FREECAD ASSEMBLY — COMPONENT RECIPES ("sway_platform")

This assembly document has 28 components, labeled P0..P27 below (a component is one placed body or linked part). 9 of them carry a construction recipe — the FreeCAD feature program that regenerates the part from scratch, quoted from this document or its linked companion documents; the rest are supplied as boundary geometry only. No exploded tour is included for this assembly.
COMPONENT P0 — geometry summary ("BK12"; no construction recipe available for this part):
  bounding box: 60.0 x 43.0 x 35.0 mm
  tessellated surface: 293,432 triangles
  volume: 48234 mm^3 (53% of its bounding box)
COMPONENT P1 — geometry summary ("DSG16H"; no construction recipe available for this part):
  bounding box: 52.0 x 40.0 x 40.0 mm
  tessellated surface: 114,100 triangles
  volume: 50009 mm^3 (60% of its bounding box)
  symmetry: mirror-symmetric across its x mid-plane
COMPONENT P2 — recipe-attached ("DSG16H_to_SH25", a linked part whose construction recipe lives in a companion FreeCAD document of the same project; that document's serialized recipe follows).
Construction recipe (the companion document, serialized — sketch geometry with constraints, then the solid features built on it; lengths are millimeters unless a unit is written):

FCSTD DOCUMENT  (FreeCAD 1.0R39109 (Git))
Label: DSG16H_to_SH25
License: All rights reserved
LicenseURL: https://en.wikipedia.org/wiki/All_rights_reserved
objects: Sketcher::SketchObject×4, PartDesign::Pocket×3, PartDesign::Pad×1, PartDesign::Fillet×1, PartDesign::Body×1
note: 24 computed .brp shape members not serialized (recipe doc carries the construction recipe); baked Part::Feature solids carry a one-line shape summary decoded from their .brp

FEATURE [Sketcher::SketchObject] Sketch
  ArcFitTolerance = 1e-06
  AttachmentSupport = -> [XY_Plane]
  FullyConstrained = true
  MakeInternals = false
  MapMode = 5
  sketch-geometry (19):
    g0: LineSegment StartX=50 StartY=0 StartZ=0 EndX=50 EndY=38 EndZ=0
    g1: LineSegment StartX=0 StartY=38 StartZ=0 EndX=0 EndY=0 EndZ=0
    g2: LineSegment [constr] StartX=5 StartY=7 StartZ=0 EndX=45 EndY=7 EndZ=0
    g3: LineSegment [constr] StartX=45 StartY=7 StartZ=0 EndX=45 EndY=31 EndZ=0
    g4: LineSegment [constr] StartX=45 StartY=31 StartZ=0 EndX=5 EndY=31 EndZ=0
    g5: LineSegment [constr] StartX=5 StartY=31 StartZ=0 EndX=5 EndY=7 EndZ=0
    g6: LineSegment [constr] StartX=0 StartY=0 StartZ=0 EndX=5 EndY=7 EndZ=0
    g7: LineSegment [constr] StartX=5 StartY=31 StartZ=0 EndX=-9e-16 EndY=38 EndZ=0
    g8: LineSegment [constr] StartX=45 StartY=31 StartZ=0 EndX=50 EndY=38 EndZ=0
    g9: Circle CenterX=5 CenterY=31 CenterZ=0 NormalX=0 NormalY=0 NormalZ=1 AngleXU=0 Radius=2.8
    g10: Circle CenterX=45 CenterY=31 CenterZ=0 NormalX=0 NormalY=0 NormalZ=1 AngleXU=0 Radius=2.8
    g11: Circle CenterX=45 CenterY=7 CenterZ=0 NormalX=0 NormalY=0 NormalZ=1 AngleXU=0 Radius=2.8
    g12: Circle CenterX=5 CenterY=7 CenterZ=0 NormalX=0 NormalY=0 NormalZ=1 AngleXU=0 Radius=2.8
    g13: LineSegment StartX=0 StartY=38 StartZ=0 EndX=13 EndY=54 EndZ=0
    g14: LineSegment StartX=13 StartY=54 StartZ=0 EndX=37 EndY=54 EndZ=0
    g15: LineSegment StartX=37 StartY=54 StartZ=0 EndX=50 EndY=38 EndZ=0
    g16: LineSegment StartX=50 StartY=0 StartZ=0 EndX=37 EndY=-16 EndZ=0
    g17: LineSegment StartX=37 StartY=-16 StartZ=0 EndX=13 EndY=-16 EndZ=0
    g18: LineSegment StartX=13 StartY=-16 StartZ=0 EndX=0 EndY=1.8e-15 EndZ=0
  constraints (49):
    c: Vertical(g0)
    c: Vertical(g1)
    c: Distance(g0,g1) = 50
    c: Distance(g1,g1) = 38
    c: Coincident(g2,g3)
    c: Coincident(g3,g4)
    c: Coincident(g4,g5)
    c: Coincident(g5,g2)
    c: Horizontal(g2)
    c: Horizontal(g4)
    c: Vertical(g3)
    c: Vertical(g5)
    c: Distance(g3,g5) = 40
    c: Distance(g2,g4) = 24
    c: Coincident(g6,g2)
    c: Coincident(g7,g4)
    c: Coincident(g8,g3)
    c: Coincident(g8,g0)
    c: Equal(g8,g7)
    c: Equal(g7,g6)
    c: Coincident(g9,g4)
    c: Coincident(g10,g3)
    c: Coincident(g11,g2)
    c: Coincident(g12,g2)
    c: Equal(g12,g9)
    c: Equal(g12,g11)
    c: Equal(g12,g10)
    c: Diameter(g12) = 5.6
    c: Equal(g0,g1)
    c: Coincident(g1,g-1)
    c: Coincident(g6,g1)
    c: PointOnObject(g0,g-1)
    c: Coincident(g7,g1)
    c: Coincident(g13,g1)
    c: Coincident(g14,g13)
    c: Horizontal(g14)
    c: Coincident(g15,g14)
    c: Coincident(g15,g0)
    c: Coincident(g16,g0)
    c: Coincident(g17,g16)
    c: Horizontal(g17)
    c: Coincident(g18,g17)
    c: Coincident(g18,g1)
    c: DistanceY(g17,g13) = 70
    c: Equal(g14,g17)
    c: Equal(g13,g15)
    c: Equal(g15,g16)
    c: Equal(g16,g18)
    c: DistanceX(g14,g14) = 24
FEATURE [PartDesign::Pad] Pad
  Direction = (0,0,1)
  Length = 12
  Length2 = 10
  Profile = -> Sketch
  ReferenceAxis = -> Sketch [N_Axis]
  Refine = true
  Suppressed = false
  Type = 0
FEATURE [Sketcher::SketchObject] Sketch001
  ArcFitTolerance = 1e-06
  AttachmentSupport = -> [Pad]
  FullyConstrained = true
  MakeInternals = false
  MapMode = 5
  Placement = pos=(0,0,12) rot=(0,0,1;0rad)
  sketch-geometry (2):
    g0: Circle CenterX=25 CenterY=47 CenterZ=0 NormalX=0 NormalY=0 NormalZ=1 AngleXU=0 Radius=3.3
    g1: Circle CenterX=25 CenterY=-9 CenterZ=0 NormalX=0 NormalY=0 NormalZ=1 AngleXU=0 Radius=3.3
  constraints (6):
    c: DistanceY(g1,g0) = 56
    c: DistanceX(g1) = 25
    c: DistanceX(g1,g0) = 0
    c: DistanceY(g1,g-1) = 9
    c: Equal(g1,g0)
    c: Diameter(g1) = 6.6
FEATURE [PartDesign::Pocket] Pocket
  BaseFeature = -> Pad
  Direction = (0,0,-1)
  Length = 5
  Length2 = 5
  Profile = -> Sketch001
  ReferenceAxis = -> Sketch001 [N_Axis]
  Refine = true
  Suppressed = false
  Type = 1
FEATURE [Sketcher::SketchObject] Sketch002
  ArcFitTolerance = 1e-06
  AttachmentSupport = -> [Pocket]
  FullyConstrained = true
  MakeInternals = false
  MapMode = 5
  Placement = pos=(0,0,0) rot=(1,0,0;3.14159rad)
  expr: Constraints[0] = Sketch001.Constraints[0]
  expr: Constraints[1] = Sketch001.Constraints[1]
  expr: Constraints[2] = Sketch001.Constraints[2]
  expr: Constraints[5] = Sketch001.Constraints[5]
  sketch-geometry (16):
    g0: Circle [constr] CenterX=25 CenterY=9 CenterZ=0 NormalX=0 NormalY=0 NormalZ=1 AngleXU=0 Radius=3.3
    g1: Circle [constr] CenterX=25 CenterY=-47 CenterZ=0 NormalX=0 NormalY=0 NormalZ=1 AngleXU=0 Radius=3.3
    g2: LineSegment StartX=27.9734 StartY=-52.15 StartZ=0 EndX=30.9467 EndY=-47 EndZ=0
    g3: LineSegment StartX=30.9467 StartY=-47 StartZ=0 EndX=27.9734 EndY=-41.85 EndZ=0
    g4: LineSegment StartX=27.9734 StartY=-41.85 StartZ=0 EndX=22.0266 EndY=-41.85 EndZ=0
    g5: LineSegment StartX=22.0266 StartY=-41.85 StartZ=0 EndX=19.0533 EndY=-47 EndZ=0
    g6: LineSegment StartX=19.0533 StartY=-47 StartZ=0 EndX=22.0266 EndY=-52.15 EndZ=0
    g7: LineSegment StartX=22.0266 StartY=-52.15 StartZ=0 EndX=27.9734 EndY=-52.15 EndZ=0
    g8: Circle [constr] CenterX=25 CenterY=-47 CenterZ=0 NormalX=0 NormalY=0 NormalZ=1 AngleXU=0 Radius=5.94671
    g9: LineSegment StartX=27.9734 StartY=3.85 StartZ=0 EndX=30.9467 EndY=9 EndZ=0
    g10: LineSegment StartX=30.9467 StartY=9 StartZ=0 EndX=27.9734 EndY=14.15 EndZ=0
    g11: LineSegment StartX=27.9734 StartY=14.15 StartZ=0 EndX=22.0266 EndY=14.15 EndZ=0
    g12: LineSegment StartX=22.0266 StartY=14.15 StartZ=0 EndX=19.0533 EndY=9 EndZ=0
    g13: LineSegment StartX=19.0533 StartY=9 StartZ=0 EndX=22.0266 EndY=3.85 EndZ=0
    g14: LineSegment StartX=22.0266 StartY=3.85 StartZ=0 EndX=27.9734 EndY=3.85 EndZ=0
    g15: Circle [constr] CenterX=25 CenterY=9 CenterZ=0 NormalX=0 NormalY=0 NormalZ=1 AngleXU=0 Radius=5.94671
  constraints (38):
    c: DistanceY(g1,g0) = 56
    c: DistanceX(g1) = 25
    c: DistanceX(g1,g0) = 0
    c: DistanceY(g1,g-1) = 47
    c: Equal(g1,g0)
    c: Diameter(g1) = 6.6
    c: Coincident(g2,g3)
    c: Coincident(g3,g4)
    c: Coincident(g4,g5)
    c: Coincident(g5,g6)
    c: Coincident(g6,g7)
    c: Coincident(g7,g2)
    c: Equal(g2, g3-g7) x5
    c: PointOnObject(g2,g8)
    c: PointOnObject(g3,g8)
    c: PointOnObject(g4,g8)
    c: PointOnObject(g5,g8)
    c: PointOnObject(g6,g8)
    c: PointOnObject(g7,g8)
    c: Coincident(g8,g1)
    c: Distance(g4,g2) = 10.3
    c: Horizontal(g4)
    c: Coincident(g9,g10)
    c: Coincident(g10,g11)
    c: Coincident(g11,g12)
    c: Coincident(g12,g13)
    c: Coincident(g13,g14)
    c: Coincident(g14,g9)
    c: Equal(g9, g10-g14) x5
    c: PointOnObject(g9,g15)
    c: PointOnObject(g10,g15)
    c: PointOnObject(g11,g15)
    c: PointOnObject(g12,g15)
    c: PointOnObject(g13,g15)
    c: PointOnObject(g14,g15)
    c: Coincident(g15,g0)
    c: Horizontal(g11)
    c: Equal(g14,g4)
FEATURE [PartDesign::Pocket] Pocket001
  BaseFeature = -> Pocket
  Direction = (0,0,1)
  Length = 6
  Length2 = 5
  Profile = -> Sketch002
  ReferenceAxis = -> Sketch002 [N_Axis]
  Refine = true
  Suppressed = false
  Type = 0
FEATURE [PartDesign::Fillet] Fillet
  Base = -> Pocket001 [Edge46,Edge44,Edge8,Edge45,Edge43,Edge5,Edge1,Edge2]
  BaseFeature = -> Pocket001
  Radius = 4
  Refine = true
  SupportTransform = false
  Suppressed = false
  UseAllEdges = false
FEATURE [Sketcher::SketchObject] Sketch003
  ArcFitTolerance = 1e-06
  AttachmentSupport = -> [Fillet]
  FullyConstrained = true
  MakeInternals = false
  MapMode = 5
  Placement = pos=(0,0,12) rot=(0,0,1;0rad)
  sketch-geometry (4):
    g0: LineSegment StartX=37 StartY=54 StartZ=0 EndX=37 EndY=-16 EndZ=0
    g1: LineSegment StartX=37 StartY=-16 StartZ=0 EndX=50 EndY=-16 EndZ=0
    g2: LineSegment StartX=50 StartY=-16 StartZ=0 EndX=50 EndY=54 EndZ=0
    g3: LineSegment StartX=50 StartY=54 StartZ=0 EndX=37 EndY=54 EndZ=0
  constraints (12):
    c: Coincident(g0,g1)
    c: Coincident(g1,g2)
    c: Coincident(g2,g3)
    c: Coincident(g3,g0)
    c: Vertical(g0)
    c: Vertical(g2)
    c: Horizontal(g1)
    c: Horizontal(g3)
    c: Distance(g0,g2) = 13
    c: DistanceX(g1) = 50
    c: DistanceY(g0) = -16
    c: DistanceY(g0,g0) = 70
FEATURE [PartDesign::Pocket] Pocket002
  BaseFeature = -> Fillet
  Direction = (0,0,-1)
  Length = 5
  Length2 = 5
  Profile = -> Sketch003
  ReferenceAxis = -> Sketch003 [N_Axis]
  Refine = true
  Suppressed = false
  Type = 0
FEATURE [PartDesign::Body] Body  label="DSG16H_to_SH25"
  AllowCompound = false
  Group = -> [Sketch,Pad,Sketch001,Pocket,Sketch002,Pocket001,Fillet,Sketch003,Pocket002]
  Origin = -> Origin
  Tip = -> Pocket002
COMPONENT P3 — geometry summary ("SC25UU_000"; no construction recipe available for this part):
  bounding box: 76.0 x 67.0 x 51.5 mm
  tessellated surface: 5,480 triangles
  volume: 179746 mm^3 (69% of its bounding box)
  symmetry: 2-fold rotationally symmetric about the z axis; mirror-symmetric across its y mid-plane
COMPONENT P4 — geometry summary ("SC25UU_001"; no construction recipe available for this part):
  bounding box: 76.0 x 67.0 x 51.5 mm
  tessellated surface: 5,480 triangles
  volume: 179746 mm^3 (69% of its bounding box)
  symmetry: 2-fold rotationally symmetric about the z axis; mirror-symmetric across its y mid-plane
COMPONENT P5 — geometry summary ("SC25UU_002"; no construction recipe available for this part):
  bounding box: 76.0 x 67.0 x 51.5 mm
  tessellated surface: 5,480 triangles
  volume: 179746 mm^3 (69% of its bounding box)
  symmetry: 2-fold rotationally symmetric about the z axis; mirror-symmetric across its y mid-plane
COMPONENT P6 — geometry summary ("SC25UU_003"; no construction recipe available for this part):
  bounding box: 76.0 x 67.0 x 51.5 mm
  tessellated surface: 5,480 triangles
  volume: 179746 mm^3 (69% of its bounding box)
  symmetry: 2-fold rotationally symmetric about the z axis; mirror-symmetric across its y mid-plane
COMPONENT P7 — recipe-attached ("SC25UU_to_SH25_001", a linked part whose construction recipe lives in a companion FreeCAD document of the same project; that document's serialized recipe follows).
Construction recipe (the companion document, serialized — sketch geometry with constraints, then the solid features built on it; lengths are millimeters unless a unit is written):

FCSTD DOCUMENT  (FreeCAD 1.0R39109 (Git))
Label: SC25UU_to_SH25
License: All rights reserved
LicenseURL: https://en.wikipedia.org/wiki/All_rights_reserved
objects: Sketcher::SketchObject×3, PartDesign::Pocket×2, PartDesign::Pad×1, PartDesign::Fillet×1, PartDesign::Body×1
note: 19 computed .brp shape members not serialized (recipe doc carries the construction recipe); baked Part::Feature solids carry a one-line shape summary decoded from their .brp

FEATURE [Sketcher::SketchObject] Sketch
  ArcFitTolerance = 1e-06
  AttachmentSupport = -> [XY_Plane]
  FullyConstrained = true
  MakeInternals = false
  MapMode = 5
  sketch-geometry (19):
    g0: LineSegment StartX=76 StartY=0 StartZ=0 EndX=76 EndY=67 EndZ=0
    g1: LineSegment StartX=0 StartY=67 StartZ=0 EndX=0 EndY=0 EndZ=0
    g2: LineSegment [constr] StartX=11 StartY=58.5 StartZ=0 EndX=11 EndY=8.5 EndZ=0
    g3: LineSegment [constr] StartX=11 StartY=8.5 StartZ=0 EndX=65 EndY=8.5 EndZ=0
    g4: LineSegment [constr] StartX=65 StartY=8.5 StartZ=0 EndX=65 EndY=58.5 EndZ=0
    g5: LineSegment [constr] StartX=65 StartY=58.5 StartZ=0 EndX=11 EndY=58.5 EndZ=0
    g6: Circle CenterX=11 CenterY=58.5 CenterZ=0 NormalX=0 NormalY=0 NormalZ=1 AngleXU=0 Radius=4.3
    g7: Circle CenterX=65 CenterY=58.5 CenterZ=0 NormalX=0 NormalY=0 NormalZ=1 AngleXU=0 Radius=4.3
    g8: Circle CenterX=65 CenterY=8.5 CenterZ=0 NormalX=0 NormalY=0 NormalZ=1 AngleXU=0 Radius=4.3
    g9: Circle CenterX=11 CenterY=8.5 CenterZ=0 NormalX=0 NormalY=0 NormalZ=1 AngleXU=0 Radius=4.3
    g10: LineSegment [constr] StartX=0 StartY=0 StartZ=0 EndX=11 EndY=8.5 EndZ=0
    g11: LineSegment [constr] StartX=65 StartY=58.5 StartZ=0 EndX=76 EndY=67 EndZ=0
    g12: LineSegment [constr] StartX=11 StartY=58.5 StartZ=0 EndX=0 EndY=67 EndZ=0
    g13: LineSegment StartX=0 StartY=67 StartZ=0 EndX=26 EndY=68.5 EndZ=0
    g14: LineSegment StartX=26 StartY=68.5 StartZ=0 EndX=50 EndY=68.5 EndZ=0
    g15: LineSegment StartX=50 StartY=68.5 StartZ=0 EndX=76 EndY=67 EndZ=0
    g16: LineSegment StartX=0 StartY=0 StartZ=0 EndX=26 EndY=-1.5 EndZ=0
    g17: LineSegment StartX=26 StartY=-1.5 StartZ=0 EndX=50 EndY=-1.5 EndZ=0
    g18: LineSegment StartX=50 StartY=-1.5 StartZ=0 EndX=76 EndY=0 EndZ=0
  constraints (49):
    c: Vertical(g0)
    c: Vertical(g1)
    c: Distance(g0,g1) = 76
    c: Distance(g1,g1) = 67
    c: Coincident(g2,g3)
    c: Coincident(g3,g4)
    c: Coincident(g4,g5)
    c: Coincident(g5,g2)
    c: Vertical(g2)
    c: Vertical(g4)
    c: Horizontal(g3)
    c: Horizontal(g5)
    c: Distance(g2,g4) = 54
    c: Distance(g3,g5) = 50
    c: Coincident(g6,g2)
    c: Coincident(g7,g4)
    c: Coincident(g8,g3)
    c: Coincident(g9,g2)
    c: Equal(g7,g8)
    c: Equal(g7,g9)
    c: Equal(g7,g6)
    c: Diameter(g7) = 8.6
    c: Coincident(g10,g2)
    c: Coincident(g11,g4)
    c: Coincident(g11,g0)
    c: Coincident(g12,g2)
    c: Equal(g12,g10)
    c: Equal(g12,g11)
    c: Coincident(g13,g1)
    c: Coincident(g14,g13)
    c: Horizontal(g14)
    c: Coincident(g15,g14)
    c: Coincident(g15,g0)
    c: Coincident(g16,g1)
    c: Coincident(g17,g16)
    c: Horizontal(g17)
    c: Coincident(g18,g17)
    c: Coincident(g18,g0)
    c: DistanceX(g17,g17) = 24
    c: Equal(g17,g14)
    c: Equal(g13,g15)
    c: Equal(g15,g18)
    c: Equal(g18,g16)
    c: Coincident(g1,g10)
    c: Coincident(g1,g-1)
    c: Coincident(g12,g1)
    c: PointOnObject(g0,g-1)
    c: Equal(g0,g1)
    c: DistanceY(g16,g13) = 70
FEATURE [PartDesign::Pad] Pad
  Direction = (0,0,1)
  Length = 10
  Length2 = 10
  Profile = -> Sketch
  ReferenceAxis = -> Sketch [N_Axis]
  Refine = true
  Suppressed = false
  Type = 0
FEATURE [Sketcher::SketchObject] Sketch001
  ArcFitTolerance = 1e-06
  AttachmentSupport = -> [Pad]
  FullyConstrained = true
  MakeInternals = false
  MapMode = 5
  Placement = pos=(0,0,10) rot=(0,0,1;0rad)
  sketch-geometry (2):
    g0: Circle CenterX=38 CenterY=61.5 CenterZ=0 NormalX=0 NormalY=0 NormalZ=1 AngleXU=0 Radius=3.3
    g1: Circle CenterX=38 CenterY=5.5 CenterZ=0 NormalX=0 NormalY=0 NormalZ=1 AngleXU=0 Radius=3.3
  constraints (6):
    c: DistanceY(g1,g0) = 56
    c: Equal(g1,g0)
    c: Diameter(g1) = 6.6
    c: DistanceY(g1) = 5.5
    c: DistanceX(g1) = 38
    c: DistanceX(g0,g1) = 0
FEATURE [PartDesign::Pocket] Pocket
  BaseFeature = -> Pad
  Direction = (0,0,-1)
  Length = 5
  Length2 = 5
  Profile = -> Sketch001
  ReferenceAxis = -> Sketch001 [N_Axis]
  Refine = true
  Suppressed = false
  Type = 1
FEATURE [Sketcher::SketchObject] Sketch002
  ArcFitTolerance = 1e-06
  AttachmentSupport = -> [Pocket]
  FullyConstrained = true
  MakeInternals = false
  MapMode = 5
  Placement = pos=(0,0,0) rot=(1,0,0;3.14159rad)
  expr: Constraints[2] = Sketch001.Constraints[2]
  expr: Constraints[4] = Sketch001.Constraints[4]
  expr: Constraints[5] = Sketch001.Constraints[5]
  sketch-geometry (16):
    g0: Circle [constr] CenterX=38 CenterY=-61.5 CenterZ=0 NormalX=0 NormalY=0 NormalZ=1 AngleXU=0 Radius=3.3
    g1: Circle [constr] CenterX=38 CenterY=-5.5 CenterZ=0 NormalX=0 NormalY=0 NormalZ=1 AngleXU=0 Radius=3.3
    g2: LineSegment StartX=40.9734 StartY=-10.65 StartZ=0 EndX=43.9467 EndY=-5.5 EndZ=0
    g3: LineSegment StartX=43.9467 StartY=-5.5 StartZ=0 EndX=40.9734 EndY=-0.35 EndZ=0
    g4: LineSegment StartX=40.9734 StartY=-0.35 StartZ=0 EndX=35.0266 EndY=-0.35 EndZ=0
    g5: LineSegment StartX=35.0266 StartY=-0.35 StartZ=0 EndX=32.0533 EndY=-5.5 EndZ=0
    g6: LineSegment StartX=32.0533 StartY=-5.5 StartZ=0 EndX=35.0266 EndY=-10.65 EndZ=0
    g7: LineSegment StartX=35.0266 StartY=-10.65 StartZ=0 EndX=40.9734 EndY=-10.65 EndZ=0
    g8: Circle [constr] CenterX=38 CenterY=-5.5 CenterZ=0 NormalX=0 NormalY=0 NormalZ=1 AngleXU=0 Radius=5.94671
    g9: LineSegment StartX=43.9467 StartY=-61.5 StartZ=0 EndX=40.9734 EndY=-56.35 EndZ=0
    g10: LineSegment StartX=40.9734 StartY=-56.35 StartZ=0 EndX=35.0266 EndY=-56.35 EndZ=0
    g11: LineSegment StartX=35.0266 StartY=-56.35 StartZ=0 EndX=32.0533 EndY=-61.5 EndZ=0
    g12: LineSegment StartX=32.0533 StartY=-61.5 StartZ=0 EndX=35.0266 EndY=-66.65 EndZ=0
    g13: LineSegment StartX=35.0266 StartY=-66.65 StartZ=0 EndX=40.9734 EndY=-66.65 EndZ=0
    g14: LineSegment StartX=40.9734 StartY=-66.65 StartZ=0 EndX=43.9467 EndY=-61.5 EndZ=0
    g15: Circle [constr] CenterX=38 CenterY=-61.5 CenterZ=0 NormalX=0 NormalY=0 NormalZ=1 AngleXU=0 Radius=5.94671
  constraints (38):
    c: DistanceY(g1,g0) = -56
    c: Equal(g1,g0)
    c: Diameter(g1) = 6.6
    c: DistanceY(g1) = -5.5
    c: DistanceX(g1) = 38
    c: DistanceX(g0,g1) = 0
    c: Coincident(g2,g3)
    c: Coincident(g3,g4)
    c: Coincident(g4,g5)
    c: Coincident(g5,g6)
    c: Coincident(g6,g7)
    c: Coincident(g7,g2)
    c: Equal(g2, g3-g7) x5
    c: PointOnObject(g2,g8)
    c: PointOnObject(g3,g8)
    c: PointOnObject(g4,g8)
    c: PointOnObject(g5,g8)
    c: PointOnObject(g6,g8)
    c: PointOnObject(g7,g8)
    c: Coincident(g8,g1)
    c: Coincident(g9,g10)
    c: Coincident(g10,g11)
    c: Coincident(g11,g12)
    c: Coincident(g12,g13)
    c: Coincident(g13,g14)
    c: Coincident(g14,g9)
    c: Equal(g9, g10-g14) x5
    c: PointOnObject(g9,g15)
    c: PointOnObject(g10,g15)
    c: PointOnObject(g11,g15)
    c: PointOnObject(g12,g15)
    c: PointOnObject(g13,g15)
    c: PointOnObject(g14,g15)
    c: Coincident(g15,g0)
    c: Distance(g10,g9) = 10.3
    c: Horizontal(g10)
    c: Equal(g10,g4)
    c: Horizontal(g4)
FEATURE [PartDesign::Pocket] Pocket001
  BaseFeature = -> Pocket
  Direction = (0,0,1)
  Length = 5.2
  Length2 = 5
  Profile = -> Sketch002
  ReferenceAxis = -> Sketch002 [N_Axis]
  Refine = true
  Suppressed = false
  Type = 0
FEATURE [PartDesign::Fillet] Fillet
  Base = -> Pocket001 [Edge1,Edge2,Edge46,Edge45]
  BaseFeature = -> Pocket001
  Radius = 3
  Refine = true
  SupportTransform = false
  Suppressed = false
  UseAllEdges = false
FEATURE [PartDesign::Body] Body  label="SC25UU_to_SH25"
  AllowCompound = false
  Group = -> [Sketch,Pad,Sketch001,Pocket,Sketch002,Pocket001,Fillet]
  Origin = -> Origin
  Tip = -> Fillet
COMPONENT P8 — same part as P7; its construction recipe is shown at P7.
COMPONENT P9 — geometry summary ("SFU1605_ball_screw_250mm"; no construction recipe available for this part):
  bounding box: 250.0 x 16.0 x 16.0 mm
  tessellated surface: 226,632 triangles
  volume: 33080 mm^3 (52% of its bounding box)
  symmetry: revolution-symmetric about the x axis through its bounding-box center
COMPONENT P10 — geometry summary ("SFU1605_ball_screw_nut"; no construction recipe available for this part):
  bounding box: 50.0 x 48.0 x 40.0 mm
  tessellated surface: 105,688 triangles
  volume: 30043 mm^3 (31% of its bounding box)
COMPONENT P11 — geometry summary ("SH25_001"; no construction recipe available for this part):
  bounding box: 70.0 x 60.0 x 24.0 mm
  tessellated surface: 3,822 triangles
  volume: 49050 mm^3 (49% of its bounding box)
COMPONENT P12 — geometry summary ("SH25_002"; no construction recipe available for this part):
  bounding box: 70.0 x 60.0 x 24.0 mm
  tessellated surface: 3,822 triangles
  volume: 49050 mm^3 (49% of its bounding box)
COMPONENT P13 — geometry summary ("SH25_003"; no construction recipe available for this part):
  bounding box: 70.0 x 60.0 x 24.0 mm
  tessellated surface: 3,822 triangles
  volume: 49050 mm^3 (49% of its bounding box)
COMPONENT P14 — geometry summary ("SH25_004"; no construction recipe available for this part):
  bounding box: 70.0 x 60.0 x 24.0 mm
  tessellated surface: 3,822 triangles
  volume: 49050 mm^3 (49% of its bounding box)
COMPONENT P15 — geometry summary ("SH25_000"; no construction recipe available for this part):
  bounding box: 70.0 x 60.0 x 24.0 mm
  tessellated surface: 3,822 triangles
  volume: 49050 mm^3 (49% of its bounding box)
COMPONENT P16 — geometry summary ("80ST-M02438"; no construction recipe available for this part):
  bounding box: 185.6 x 92.0 x 80.0 mm
  tessellated surface: 30,310 triangles
  volume: 810178 mm^3 (59% of its bounding box)
COMPONENT P17 — recipe-attached ("coupler_10x19", a linked part whose construction recipe lives in a companion FreeCAD document of the same project; that document's serialized recipe follows).
Construction recipe (the companion document, serialized — sketch geometry with constraints, then the solid features built on it; lengths are millimeters unless a unit is written):

FCSTD DOCUMENT  (FreeCAD 1.0R39109 (Git))
Label: coupler
License: All rights reserved
LicenseURL: https://en.wikipedia.org/wiki/All_rights_reserved
objects: Sketcher::SketchObject×3, PartDesign::Pocket×2, PartDesign::Pad×1, PartDesign::Body×1
note: 16 computed .brp shape members not serialized (recipe doc carries the construction recipe); baked Part::Feature solids carry a one-line shape summary decoded from their .brp

FEATURE [Sketcher::SketchObject] Sketch
  ArcFitTolerance = 1e-06
  AttachmentSupport = -> [XZ_Plane]
  FullyConstrained = true
  MakeInternals = false
  MapMode = 5
  Placement = pos=(0,0,0) rot=(1,0,0;1.5708rad)
  sketch-geometry (1):
    g0: Circle CenterX=0 CenterY=0 CenterZ=0 NormalX=0 NormalY=0 NormalZ=1 AngleXU=0 Radius=17.5
  constraints (2):
    c: Coincident(g0,g-1)
    c: Diameter(g0) = 35
FEATURE [PartDesign::Pad] Pad
  Direction = (0,-1,2e-16)
  Length = 50
  Length2 = 10
  Placement = pos=(0,0,0) rot=(1,0,0;1.5708rad)
  Profile = -> Sketch
  ReferenceAxis = -> Sketch [N_Axis]
  Refine = true
  Suppressed = false
  Type = 0
FEATURE [Sketcher::SketchObject] Sketch001
  ArcFitTolerance = 1e-06
  AttachmentSupport = -> [Pad]
  FullyConstrained = true
  MakeInternals = false
  MapMode = 5
  Placement = pos=(0,-50,0) rot=(1,0,0;1.5708rad)
  sketch-geometry (1):
    g0: Circle CenterX=0 CenterY=0 CenterZ=0 NormalX=0 NormalY=0 NormalZ=1 AngleXU=0 Radius=9.5
  constraints (2):
    c: Coincident(g0,g-1)
    c: Diameter(g0) = 19
FEATURE [PartDesign::Pocket] Pocket
  BaseFeature = -> Pad
  Direction = (0,1,-2e-16)
  Length = 18.5
  Length2 = 5
  Placement = pos=(0,0,0) rot=(1,0,0;1.5708rad)
  Profile = -> Sketch001
  ReferenceAxis = -> Sketch001 [N_Axis]
  Refine = true
  Suppressed = false
  Type = 0
FEATURE [Sketcher::SketchObject] Sketch002
  ArcFitTolerance = 1e-06
  AttachmentSupport = -> [Pocket]
  FullyConstrained = true
  MakeInternals = false
  MapMode = 5
  Placement = pos=(0,0,0) rot=(-1,0,0;1.5708rad)
  sketch-geometry (1):
    g0: Circle CenterX=0 CenterY=0 CenterZ=0 NormalX=0 NormalY=0 NormalZ=1 AngleXU=0 Radius=5
  constraints (2):
    c: Diameter(g0) = 10
    c: Coincident(g0,g-1)
FEATURE [PartDesign::Pocket] Pocket001
  BaseFeature = -> Pocket
  Direction = (0,-1,-2e-16)
  Length = 18.5
  Length2 = 5
  Placement = pos=(0,0,0) rot=(1,0,0;1.5708rad)
  Profile = -> Sketch002
  ReferenceAxis = -> Sketch002 [N_Axis]
  Refine = true
  Suppressed = false
  Type = 0
FEATURE [PartDesign::Body] Body  label="coupler_10x19"
  AllowCompound = false
  Group = -> [Sketch,Pad,Sketch001,Pocket,Sketch002,Pocket001]
  Origin = -> Origin
  Tip = -> Pocket001
COMPONENT P18 — recipe-attached ("linear_shaft_25x428_front", a linked part whose construction recipe lives in a companion FreeCAD document of the same project; that document's serialized recipe follows).
Construction recipe (the companion document, serialized — sketch geometry with constraints, then the solid features built on it; lengths are millimeters unless a unit is written):

FCSTD DOCUMENT  (FreeCAD 1.0R39109 (Git))
Label: linear_shaft
License: All rights reserved
LicenseURL: https://en.wikipedia.org/wiki/All_rights_reserved
objects: Sketcher::SketchObject×2, PartDesign::Pad×2, PartDesign::Body×2
note: 12 computed .brp shape members not serialized (recipe doc carries the construction recipe); baked Part::Feature solids carry a one-line shape summary decoded from their .brp

FEATURE [Sketcher::SketchObject] Sketch
  ArcFitTolerance = 1e-06
  AttachmentSupport = -> [XZ_Plane]
  FullyConstrained = true
  MakeInternals = false
  MapMode = 5
  Placement = pos=(0,0,0) rot=(1,0,0;1.5708rad)
  sketch-geometry (1):
    g0: Circle CenterX=0 CenterY=0 CenterZ=0 NormalX=0 NormalY=0 NormalZ=1 AngleXU=0 Radius=12.5
  constraints (2):
    c: Diameter(g0) = 25
    c: Coincident(g0,g-1)
FEATURE [PartDesign::Pad] Pad
  Direction = (0,-1,2e-16)
  Length = 500
  Length2 = 10
  Placement = pos=(0,0,0) rot=(1,0,0;1.5708rad)
  Profile = -> Sketch
  ReferenceAxis = -> Sketch [N_Axis]
  Refine = true
  Suppressed = false
  Type = 0
FEATURE [PartDesign::Body] Body  label="linear_shaft_25x500"
  AllowCompound = false
  Group = -> [Sketch,Pad]
  Origin = -> Origin
  Tip = -> Pad
FEATURE [Sketcher::SketchObject] Sketch001
  ArcFitTolerance = 1e-06
  AttachmentSupport = -> [XZ_Plane001]
  FullyConstrained = true
  MakeInternals = false
  MapMode = 5
  Placement = pos=(0,0,0) rot=(1,0,0;1.5708rad)
  sketch-geometry (1):
    g0: Circle CenterX=0 CenterY=0 CenterZ=0 NormalX=0 NormalY=0 NormalZ=1 AngleXU=0 Radius=12.5
  constraints (2):
    c: Diameter(g0) = 25
    c: Coincident(g0,g-1)
FEATURE [PartDesign::Pad] Pad001
  Direction = (0,-1,2e-16)
  Length = 428
  Length2 = 10
  Placement = pos=(0,0,0) rot=(1,0,0;1.5708rad)
  Profile = -> Sketch001
  ReferenceAxis = -> Sketch001 [N_Axis]
  Refine = true
  Suppressed = false
  Type = 0
FEATURE [PartDesign::Body] Body001  label="linear_shaft_25x428"
  AllowCompound = false
  Group = -> [Sketch001,Pad001]
  Origin = -> Origin001
  Tip = -> Pad001
COMPONENT P19 — same part as P18; its construction recipe is shown at P18.
COMPONENT P20 — geometry summary ("sway_SC25UU_to_SH25_with_plate_001"; no construction recipe available for this part):
  bounding box: 76.0 x 70.0 x 10.0 mm
  tessellated surface: 3,376 triangles
  volume: 40438 mm^3 (76% of its bounding box)
COMPONENT P21 — geometry summary ("sway_SC25UU_to_SH25_with_plate_000"; no construction recipe available for this part):
  bounding box: 76.0 x 70.0 x 10.0 mm
  tessellated surface: 3,376 triangles
  volume: 40438 mm^3 (76% of its bounding box)
COMPONENT P22 — recipe-attached ("sway_motor_mount_bottom", a linked part whose construction recipe lives in a companion FreeCAD document of the same project; that document's serialized recipe follows).
Construction recipe (the companion document, serialized — sketch geometry with constraints, then the solid features built on it; lengths are millimeters unless a unit is written):

FCSTD DOCUMENT  (FreeCAD 1.0R39109 (Git))
Label: sway_motor_mount_bottom
License: All rights reserved
LicenseURL: https://en.wikipedia.org/wiki/All_rights_reserved
objects: Sketcher::SketchObject×3, PartDesign::Pocket×2, PartDesign::Fillet×2, PartDesign::Pad×1, PartDesign::Body×1
note: 22 computed .brp shape members not serialized (recipe doc carries the construction recipe); baked Part::Feature solids carry a one-line shape summary decoded from their .brp

FEATURE [Sketcher::SketchObject] Sketch
  ArcFitTolerance = 1e-06
  AttachmentSupport = -> [XZ_Plane]
  FullyConstrained = true
  MakeInternals = false
  MapMode = 5
  Placement = pos=(0,0,0) rot=(1,0,0;1.5708rad)
  sketch-geometry (30):
    g0: LineSegment [constr] StartX=-66.2 StartY=5 StartZ=0 EndX=-66.2 EndY=-5 EndZ=0
    g1: LineSegment [constr] StartX=-66.2 StartY=-5 StartZ=0 EndX=-40 EndY=-5 EndZ=0
    g2: LineSegment [constr] StartX=-40 StartY=-5 StartZ=0 EndX=-40 EndY=5 EndZ=0
    g3: LineSegment [constr] StartX=-40 StartY=5 StartZ=0 EndX=-66.2 EndY=5 EndZ=0
    g4: LineSegment [constr] StartX=40 StartY=5 StartZ=0 EndX=40 EndY=-5 EndZ=0
    g5: LineSegment [constr] StartX=40 StartY=-5 StartZ=0 EndX=66.2 EndY=-5 EndZ=0
    g6: LineSegment [constr] StartX=66.2 StartY=-5 StartZ=0 EndX=66.2 EndY=5 EndZ=0
    g7: LineSegment [constr] StartX=66.2 StartY=5 StartZ=0 EndX=40 EndY=5 EndZ=0
    g8: LineSegment [constr] StartX=-40 StartY=-5 StartZ=0 EndX=0 EndY=0 EndZ=0
    g9: LineSegment [constr] StartX=0 StartY=0 StartZ=0 EndX=40 EndY=-5 EndZ=0
    g10: LineSegment [constr] StartX=-40 StartY=60 StartZ=0 EndX=-40 EndY=-20 EndZ=0
    g11: LineSegment [constr] StartX=-40 StartY=-20 StartZ=0 EndX=40 EndY=-20 EndZ=0
    g12: LineSegment [constr] StartX=40 StartY=-20 StartZ=0 EndX=40 EndY=60 EndZ=0
    g13: LineSegment [constr] StartX=40 StartY=60 StartZ=0 EndX=-40 EndY=60 EndZ=0
    g14: LineSegment StartX=40.4 StartY=-5.4 StartZ=0 EndX=65.4 EndY=-5.4 EndZ=0
    g15: LineSegment StartX=65.4 StartY=-5.4 StartZ=0 EndX=65.4 EndY=-15.4 EndZ=0
    g16: LineSegment StartX=-65.4 StartY=-15.4 StartZ=0 EndX=-65.4 EndY=-5.4 EndZ=0
    g17: LineSegment StartX=-65.4 StartY=-5.4 StartZ=0 EndX=-40.4 EndY=-5.4 EndZ=0
    g18: ArcOfCircle [constr] CenterX=-40 CenterY=-20 CenterZ=0 NormalX=0 NormalY=0 NormalZ=1 AngleXU=0 Radius=14 StartAngle=0 EndAngle=1.5708
    g19: ArcOfCircle [constr] CenterX=-40 CenterY=60 CenterZ=0 NormalX=0 NormalY=0 NormalZ=1 AngleXU=0 Radius=14 StartAngle=4.71239 EndAngle=6.28319
    g20: ArcOfCircle [constr] CenterX=40 CenterY=-20 CenterZ=0 NormalX=0 NormalY=0 NormalZ=1 AngleXU=0 Radius=14 StartAngle=1.5708 EndAngle=3.14159
    g21: ArcOfCircle [constr] CenterX=40 CenterY=60 CenterZ=0 NormalX=0 NormalY=0 NormalZ=1 AngleXU=0 Radius=14 StartAngle=3.14159 EndAngle=4.71239
    g22: ArcOfCircle CenterX=-40.4 CenterY=-20.4 CenterZ=0 NormalX=0 NormalY=0 NormalZ=1 AngleXU=0 Radius=14 StartAngle=0 EndAngle=1.5708
    g23: ArcOfCircle CenterX=40.4 CenterY=-20.4 CenterZ=0 NormalX=0 NormalY=0 NormalZ=1 AngleXU=0 Radius=14 StartAngle=1.5708 EndAngle=3.14159
    g24: LineSegment StartX=-40.4 StartY=-6.4 StartZ=0 EndX=-40.4 EndY=-5.4 EndZ=0
    g25: LineSegment StartX=-26.4 StartY=-20.4 StartZ=0 EndX=26.4 EndY=-20.4 EndZ=0
    g26: LineSegment StartX=40.4 StartY=-6.4 StartZ=0 EndX=40.4 EndY=-5.4 EndZ=0
    g27: LineSegment StartX=-65.4 StartY=-15.4 StartZ=0 EndX=-26.4 EndY=-25.4 EndZ=0
    g28: LineSegment StartX=-26.4 StartY=-25.4 StartZ=0 EndX=26.4 EndY=-25.4 EndZ=0
    g29: LineSegment StartX=26.4 StartY=-25.4 StartZ=0 EndX=65.4 EndY=-15.4 EndZ=0
  constraints (94):
    c: Coincident(g0,g1)
    c: Coincident(g1,g2)
    c: Coincident(g2,g3)
    c: Coincident(g3,g0)
    c: Vertical(g0)
    c: Vertical(g2)
    c: Horizontal(g1)
    c: Horizontal(g3)
    c: Coincident(g4,g5)
    c: Coincident(g5,g6)
    c: Coincident(g6,g7)
    c: Coincident(g7,g4)
    c: Vertical(g4)
    c: Vertical(g6)
    c: Horizontal(g5)
    c: Horizontal(g7)
    c: Equal(g2,g4)
    c: DistanceY(g0,g0) = 10
    c: DistanceX(g2,g4) = 80
    c: DistanceY(g2,g4) = 0
    c: Coincident(g8,g1)
    c: Coincident(g8,g-1)
    c: Coincident(g9,g8)
    c: Coincident(g9,g4)
    c: Equal(g9,g8)
    c: Coincident(g10,g11)
    c: Coincident(g11,g12)
    c: Coincident(g12,g13)
    c: Coincident(g13,g10)
    c: Vertical(g10)
    c: Vertical(g12)
    c: Horizontal(g11)
    c: Horizontal(g13)
    c: PointOnObject(g2,g10)
    c: PointOnObject(g4,g12)
    c: Equal(g13,g10)
    c: DistanceY(g2) = 5
    c: Horizontal(g14)
    c: Coincident(g14,g15)
    c: Vertical(g15)
    c: Vertical(g16)
    c: Coincident(g16,g17)
    c: Horizontal(g17)
    c: DistanceY(g17,g1) = 0.4
    c: Equal(g16,g15)
    c: DistanceY(g16,g16) = 10
    c: Coincident(g18,g10)
    c: PointOnObject(g18,g10)
    c: PointOnObject(g18,g11)
    c: Diameter(g18) = 28
    c: Coincident(g19,g10)
    c: PointOnObject(g19,g13)
    c: PointOnObject(g19,g10)
    c: Coincident(g20,g11)
    c: PointOnObject(g20,g11)
    c: PointOnObject(g20,g12)
    c: Coincident(g21,g12)
    c: PointOnObject(g21,g13)
    c: PointOnObject(g21,g12)
    c: Equal(g18,g20)
    c: Equal(g20,g21)
    c: Equal(g21,g19)
    c: DistanceX(g17,g1) = 0.4
    c: Coincident(g24,g22)
    c: Coincident(g24,g17)
    c: Vertical(g24)
    c: DistanceY(g22,g18) = 0.4
    c: Coincident(g25,g22)
    c: Coincident(g25,g23)
    c: Horizontal(g25)
    c: DistanceY(g22,g18) = 0.4
    c: Perpendicular(g22,g24)
    c: Perpendicular(g22,g25)
    c: Perpendicular(g23,g25)
    c: Coincident(g26,g23)
    c: Coincident(g26,g14)
    c: Vertical(g26)
    c: Equal(g17,g14)
    c: Equal(g24,g26)
    c: Coincident(g16,g27)
    c: Coincident(g27,g28)
    c: Horizontal(g28)
    c: Coincident(g28,g29)
    c: Coincident(g29,g15)
    c: DistanceX(g27,g22) = 0
    c: DistanceY(g27,g22) = 5
    c: DistanceX(g28,g23) = 0
    c: Equal(g29,g27)
    c: DistanceX(g4,g14) = 0.4
    c: DistanceY(g14,g4) = 0.4
    c: Equal(g3,g7)
    c: DistanceX(g3,g3) = 26.2
    c: DistanceX(g17,g17) = 25
    c: DistanceY(g18,g1) = 15
FEATURE [PartDesign::Pad] Pad
  Direction = (0,-1,2e-16)
  Length = 25
  Length2 = 10
  Placement = pos=(0,0,0) rot=(1,0,0;1.5708rad)
  Profile = -> Sketch
  ReferenceAxis = -> Sketch [N_Axis]
  Refine = true
  Suppressed = false
  Type = 0
FEATURE [Sketcher::SketchObject] Sketch001
  ArcFitTolerance = 1e-06
  AttachmentSupport = -> [Pad]
  FullyConstrained = true
  MakeInternals = false
  MapMode = 5
  Placement = pos=(0,-1.2e-15,-5.4) rot=(0,0,1;3.14159rad)
  sketch-geometry (14):
    g0: LineSegment [constr] StartX=-65.4 StartY=0 StartZ=0 EndX=-40.4 EndY=0 EndZ=0
    g1: LineSegment [constr] StartX=-40.4 StartY=0 StartZ=0 EndX=-40.4 EndY=25 EndZ=0
    g2: LineSegment [constr] StartX=-40.4 StartY=25 StartZ=0 EndX=-65.4 EndY=25 EndZ=0
    g3: LineSegment [constr] StartX=-65.4 StartY=25 StartZ=0 EndX=-65.4 EndY=0 EndZ=0
    g4: LineSegment [constr] StartX=65.4 StartY=0 StartZ=0 EndX=65.4 EndY=25 EndZ=0
    g5: LineSegment [constr] StartX=65.4 StartY=25 StartZ=0 EndX=40.4 EndY=25 EndZ=0
    g6: LineSegment [constr] StartX=40.4 StartY=25 StartZ=0 EndX=40.4 EndY=0 EndZ=0
    g7: LineSegment [constr] StartX=40.4 StartY=0 StartZ=0 EndX=65.4 EndY=0 EndZ=0
    g8: LineSegment [constr] StartX=-65.4 StartY=25 StartZ=0 EndX=-40.4 EndY=0 EndZ=0
    g9: LineSegment [constr] StartX=-65.4 StartY=0 StartZ=0 EndX=-40.4 EndY=25 EndZ=0
    g10: LineSegment [constr] StartX=40.4 StartY=25 StartZ=0 EndX=65.4 EndY=0 EndZ=0
    g11: LineSegment [constr] StartX=40.4 StartY=0 StartZ=0 EndX=65.4 EndY=25 EndZ=0
    g12: Circle CenterX=-52.9 CenterY=12.5 CenterZ=0 NormalX=0 NormalY=0 NormalZ=1 AngleXU=0 Radius=4.3
    g13: Circle CenterX=52.9 CenterY=12.5 CenterZ=0 NormalX=0 NormalY=0 NormalZ=1 AngleXU=0 Radius=4.3
  constraints (36):
    c: Coincident(g0,g1)
    c: Coincident(g1,g2)
    c: Coincident(g2,g3)
    c: Coincident(g3,g0)
    c: Horizontal(g0)
    c: Horizontal(g2)
    c: Vertical(g1)
    c: Vertical(g3)
    c: Distance(g1,g3) = 25
    c: Distance(g0,g2) = 25
    c: PointOnObject(g0,g-1)
    c: DistanceX(g0) = -40.4
    c: Coincident(g4,g5)
    c: Coincident(g5,g6)
    c: Coincident(g6,g7)
    c: Coincident(g7,g4)
    c: Vertical(g4)
    c: Vertical(g6)
    c: Horizontal(g5)
    c: Horizontal(g7)
    c: PointOnObject(g4,g-1)
    c: Equal(g6,g5)
    c: Equal(g5,g1)
    c: DistanceX(g6) = 40.4
    c: Coincident(g8,g2)
    c: Coincident(g8,g0)
    c: Coincident(g9,g0)
    c: Coincident(g9,g1)
    c: Coincident(g10,g5)
    c: Coincident(g10,g4)
    c: Coincident(g11,g6)
    c: Coincident(g11,g4)
    c: Diameter(g12) = 8.6
    c: Symmetric(g8,g8,g12)
    c: Symmetric(g11,g11,g13)
    c: Equal(g13,g12)
FEATURE [PartDesign::Pocket] Pocket
  BaseFeature = -> Pad
  Direction = (0,0,-1)
  Length = 5
  Length2 = 5
  Placement = pos=(0,0,0) rot=(1,0,0;1.5708rad)
  Profile = -> Sketch001
  ReferenceAxis = -> Sketch001 [N_Axis]
  Refine = true
  Suppressed = false
  Type = 1
FEATURE [Sketcher::SketchObject] Sketch002
  ArcFitTolerance = 1e-06
  AttachmentOffset = pos=(0,0,-5) rot=(0,0,1;0rad)
  AttachmentSupport = -> [Pocket]
  FullyConstrained = true
  MakeInternals = false
  MapMode = 5
  Placement = pos=(0,-1.2e-15,-10.4) rot=(0,0,1;3.14159rad)
  expr: Constraints[11] = Sketch001.Constraints[11]
  expr: Constraints[23] = Sketch001.Constraints[23]
  expr: Constraints[32] = Sketch001.Constraints[32]
  expr: Constraints[8] = Sketch001.Constraints[8]
  expr: Constraints[9] = Sketch001.Constraints[9]
  sketch-geometry (28):
    g0: LineSegment [constr] StartX=-65.4 StartY=0 StartZ=0 EndX=-40.4 EndY=0 EndZ=0
    g1: LineSegment [constr] StartX=-40.4 StartY=0 StartZ=0 EndX=-40.4 EndY=25 EndZ=0
    g2: LineSegment [constr] StartX=-40.4 StartY=25 StartZ=0 EndX=-65.4 EndY=25 EndZ=0
    g3: LineSegment [constr] StartX=-65.4 StartY=25 StartZ=0 EndX=-65.4 EndY=0 EndZ=0
    g4: LineSegment [constr] StartX=65.4 StartY=0 StartZ=0 EndX=65.4 EndY=25 EndZ=0
    g5: LineSegment [constr] StartX=65.4 StartY=25 StartZ=0 EndX=40.4 EndY=25 EndZ=0
    g6: LineSegment [constr] StartX=40.4 StartY=25 StartZ=0 EndX=40.4 EndY=0 EndZ=0
    g7: LineSegment [constr] StartX=40.4 StartY=0 StartZ=0 EndX=65.4 EndY=0 EndZ=0
    g8: LineSegment [constr] StartX=-65.4 StartY=25 StartZ=0 EndX=-40.4 EndY=0 EndZ=0
    g9: LineSegment [constr] StartX=-65.4 StartY=0 StartZ=0 EndX=-40.4 EndY=25 EndZ=0
    g10: LineSegment [constr] StartX=40.4 StartY=25 StartZ=0 EndX=65.4 EndY=0 EndZ=0
    g11: LineSegment [constr] StartX=40.4 StartY=0 StartZ=0 EndX=65.4 EndY=25 EndZ=0
    g12: Circle [constr] CenterX=-52.9 CenterY=12.5 CenterZ=0 NormalX=0 NormalY=0 NormalZ=1 AngleXU=0 Radius=4.3
    g13: Circle [constr] CenterX=52.9 CenterY=12.5 CenterZ=0 NormalX=0 NormalY=0 NormalZ=1 AngleXU=0 Radius=4.3
    g14: LineSegment StartX=-46.3 StartY=8.68949 StartZ=0 EndX=-46.3 EndY=16.3105 EndZ=0
    g15: LineSegment StartX=-46.3 StartY=16.3105 StartZ=0 EndX=-52.9 EndY=20.121 EndZ=0
    g16: LineSegment StartX=-52.9 StartY=20.121 StartZ=0 EndX=-59.5 EndY=16.3105 EndZ=0
    g17: LineSegment StartX=-59.5 StartY=16.3105 StartZ=0 EndX=-59.5 EndY=8.68949 EndZ=0
    g18: LineSegment StartX=-59.5 StartY=8.68949 StartZ=0 EndX=-52.9 EndY=4.87898 EndZ=0
    g19: LineSegment StartX=-52.9 StartY=4.87898 StartZ=0 EndX=-46.3 EndY=8.68949 EndZ=0
    g20: Circle [constr] CenterX=-52.9 CenterY=12.5 CenterZ=0 NormalX=0 NormalY=0 NormalZ=1 AngleXU=0 Radius=7.62102
    g21: LineSegment StartX=59.5 StartY=8.68949 StartZ=0 EndX=59.5 EndY=16.3105 EndZ=0
    g22: LineSegment StartX=59.5 StartY=16.3105 StartZ=0 EndX=52.9 EndY=20.121 EndZ=0
    g23: LineSegment StartX=52.9 StartY=20.121 StartZ=0 EndX=46.3 EndY=16.3105 EndZ=0
    g24: LineSegment StartX=46.3 StartY=16.3105 StartZ=0 EndX=46.3 EndY=8.68949 EndZ=0
    g25: LineSegment StartX=46.3 StartY=8.68949 StartZ=0 EndX=52.9 EndY=4.87898 EndZ=0
    g26: LineSegment StartX=52.9 StartY=4.87898 StartZ=0 EndX=59.5 EndY=8.68949 EndZ=0
    g27: Circle [constr] CenterX=52.9 CenterY=12.5 CenterZ=0 NormalX=0 NormalY=0 NormalZ=1 AngleXU=0 Radius=7.62102
  constraints (68):
    c: Coincident(g0,g1)
    c: Coincident(g1,g2)
    c: Coincident(g2,g3)
    c: Coincident(g3,g0)
    c: Horizontal(g0)
    c: Horizontal(g2)
    c: Vertical(g1)
    c: Vertical(g3)
    c: Distance(g1,g3) = 25
    c: Distance(g0,g2) = 25
    c: PointOnObject(g0,g-1)
    c: DistanceX(g0) = -40.4
    c: Coincident(g4,g5)
    c: Coincident(g5,g6)
    c: Coincident(g6,g7)
    c: Coincident(g7,g4)
    c: Vertical(g4)
    c: Vertical(g6)
    c: Horizontal(g5)
    c: Horizontal(g7)
    c: PointOnObject(g4,g-1)
    c: Equal(g6,g5)
    c: Equal(g5,g1)
    c: DistanceX(g6) = 40.4
    c: Coincident(g8,g2)
    c: Coincident(g8,g0)
    c: Coincident(g9,g0)
    c: Coincident(g9,g1)
    c: Coincident(g10,g5)
    c: Coincident(g10,g4)
    c: Coincident(g11,g6)
    c: Coincident(g11,g4)
    c: Diameter(g12) = 8.6
    c: Symmetric(g8,g8,g12)
    c: Symmetric(g11,g11,g13)
    c: Equal(g13,g12)
    c: Coincident(g14,g15)
    c: Coincident(g15,g16)
    c: Coincident(g16,g17)
    c: Coincident(g17,g18)
    c: Coincident(g18,g19)
    c: Coincident(g19,g14)
    c: Equal(g14, g15-g19) x5
    c: PointOnObject(g14,g20)
    c: PointOnObject(g15,g20)
    c: PointOnObject(g16,g20)
    c: PointOnObject(g17,g20)
    c: PointOnObject(g18,g20)
    c: PointOnObject(g19,g20)
    c: Coincident(g20,g12)
    c: Vertical(g17)
    c: DistanceX(g16,g14) = 13.2
    c: Coincident(g21,g22)
    c: Coincident(g22,g23)
    c: Coincident(g23,g24)
    c: Coincident(g24,g25)
    c: Coincident(g25,g26)
    c: Coincident(g26,g21)
    c: Equal(g21, g22-g26) x5
    c: PointOnObject(g21,g27)
    c: PointOnObject(g22,g27)
    c: PointOnObject(g23,g27)
    c: PointOnObject(g24,g27)
    c: PointOnObject(g25,g27)
    c: PointOnObject(g26,g27)
    c: Coincident(g27,g13)
    c: Vertical(g21)
    c: Equal(g16,g23)
FEATURE [PartDesign::Pocket] Pocket001
  BaseFeature = -> Pocket
  Direction = (0,0,-1)
  Length = 5
  Length2 = 5
  Placement = pos=(0,0,0) rot=(1,0,0;1.5708rad)
  Profile = -> Sketch002
  ReferenceAxis = -> Sketch002 [N_Axis]
  Refine = true
  Suppressed = false
  Type = 1
FEATURE [PartDesign::Fillet] Fillet
  Base = -> Pocket001 [Edge25,Edge16,Edge21,Edge12]
  BaseFeature = -> Pocket001
  Placement = pos=(0,0,0) rot=(1,0,0;1.5708rad)
  Radius = 4
  Refine = true
  SupportTransform = false
  Suppressed = false
  UseAllEdges = false
FEATURE [PartDesign::Fillet] Fillet001
  Base = -> Fillet [Edge46,Edge38]
  BaseFeature = -> Fillet
  Placement = pos=(0,0,0) rot=(1,0,0;1.5708rad)
  Radius = 18
  Refine = true
  SupportTransform = false
  Suppressed = false
  UseAllEdges = false
FEATURE [PartDesign::Body] Body  label="sway_motor_mount_bottom"
  AllowCompound = false
  Group = -> [Sketch,Pad,Sketch001,Pocket,Sketch002,Pocket001,Fillet,Fillet001]
  Origin = -> Origin
  Tip = -> Fillet001
COMPONENT P23 — geometry summary ("sway_motor_mount_front_plate"; no construction recipe available for this part):
  bounding box: 221.0 x 96.6 x 45.0 mm
  tessellated surface: 3,504 triangles
  volume: 113260 mm^3 (12% of its bounding box)
COMPONENT P24 — geometry summary ("sway_motor_mount_front_plate_shaft_support"; no construction recipe available for this part):
  bounding box: 82.5 x 41.8 x 24.0 mm
  tessellated surface: 17,200 triangles
  volume: 35421 mm^3 (43% of its bounding box)
  symmetry: mirror-symmetric across its x mid-plane
COMPONENT P25 — recipe-attached ("sway_motor_mount_rear_plate", a linked part whose construction recipe lives in a companion FreeCAD document of the same project; that document's serialized recipe follows).
Construction recipe (the companion document, serialized — sketch geometry with constraints, then the solid features built on it; lengths are millimeters unless a unit is written):

FCSTD DOCUMENT  (FreeCAD 1.0R39109 (Git))
Label: sway_motor_mount_rear_plate
License: All rights reserved
LicenseURL: https://en.wikipedia.org/wiki/All_rights_reserved
objects: Sketcher::SketchObject×3, PartDesign::Pocket×2, PartDesign::Pad×1, PartDesign::Fillet×1, PartDesign::Body×1
note: 19 computed .brp shape members not serialized (recipe doc carries the construction recipe); baked Part::Feature solids carry a one-line shape summary decoded from their .brp

FEATURE [Sketcher::SketchObject] Sketch
  ArcFitTolerance = 1e-06
  AttachmentSupport = -> [XY_Plane]
  FullyConstrained = true
  MakeInternals = false
  MapMode = 5
  sketch-geometry (20):
    g0: LineSegment [constr] StartX=0 StartY=0 StartZ=0 EndX=178 EndY=0 EndZ=0
    g1: LineSegment [constr] StartX=178 StartY=0 StartZ=0 EndX=178 EndY=70 EndZ=0
    g2: LineSegment [constr] StartX=178 StartY=70 StartZ=0 EndX=0 EndY=70 EndZ=0
    g3: LineSegment [constr] StartX=0 StartY=70 StartZ=0 EndX=0 EndY=0 EndZ=0
    g4: Circle CenterX=15 CenterY=60 CenterZ=0 NormalX=0 NormalY=0 NormalZ=1 AngleXU=0 Radius=4.3
    g5: Circle CenterX=15 CenterY=10 CenterZ=0 NormalX=0 NormalY=0 NormalZ=1 AngleXU=0 Radius=4.3
    g6: Circle CenterX=170 CenterY=47 CenterZ=0 NormalX=0 NormalY=0 NormalZ=1 AngleXU=0 Radius=2.8
    g7: Circle CenterX=170 CenterY=23 CenterZ=0 NormalX=0 NormalY=0 NormalZ=1 AngleXU=0 Radius=2.8
    g8: LineSegment StartX=0.4 StartY=0 StartZ=0 EndX=177.6 EndY=0 EndZ=0
    g9: LineSegment StartX=177.6 StartY=0 StartZ=0 EndX=177.6 EndY=70 EndZ=0
    g10: LineSegment StartX=0.4 StartY=70.4 StartZ=0 EndX=0.4 EndY=0 EndZ=0
    g11: LineSegment [constr] StartX=-19 StartY=97 StartZ=0 EndX=95.6 EndY=97 EndZ=0
    g12: LineSegment [constr] StartX=95.6 StartY=97 StartZ=0 EndX=95.6 EndY=177 EndZ=0
    g13: LineSegment [constr] StartX=95.6 StartY=177 StartZ=0 EndX=-19 EndY=177 EndZ=0
    g14: LineSegment [constr] StartX=-19 StartY=177 StartZ=0 EndX=-19 EndY=97 EndZ=0
    g15: LineSegment StartX=0.4 StartY=70.4 StartZ=0 EndX=-19 EndY=70.4 EndZ=0
    g16: LineSegment StartX=-19 StartY=70.4 StartZ=0 EndX=-19 EndY=96.6 EndZ=0
    g17: LineSegment StartX=-19 StartY=96.6 StartZ=0 EndX=115.6 EndY=96.6 EndZ=0
    g18: LineSegment StartX=115.6 StartY=96.6 StartZ=0 EndX=115.6 EndY=70 EndZ=0
    g19: LineSegment StartX=115.6 StartY=70 StartZ=0 EndX=177.6 EndY=70 EndZ=0
  constraints (59):
    c: Coincident(g0,g1)
    c: Coincident(g1,g2)
    c: Coincident(g2,g3)
    c: Coincident(g3,g0)
    c: Horizontal(g0)
    c: Horizontal(g2)
    c: Vertical(g1)
    c: Vertical(g3)
    c: Distance(g1,g3) = 178
    c: Distance(g0,g2) = 70
    c: Coincident(g0,g-1)
    c: DistanceX(g5) = 15
    c: DistanceX(g5,g4) = 0
    c: DistanceY(g5,g4) = 50
    c: Equal(g5,g4)
    c: Diameter(g5) = 8.6
    c: DistanceY(g0,g5) = 10
    c: DistanceX(g7,g0) = 8
    c: DistanceY(g7,g6) = 24
    c: DistanceX(g6,g7) = 0
    c: Diameter(g7) = 5.6
    c: Equal(g7,g6)
    c: DistanceY(g7) = 23
    c: Coincident(g8,g9)
    c: Coincident(g10,g8)
    c: Horizontal(g8)
    c: Vertical(g9)
    c: Vertical(g10)
    c: DistanceX(g8) = 0.4
    c: PointOnObject(g8,g-1)
    c: DistanceX(g8,g0) = 0.4
    c: Coincident(g11,g12)
    c: Coincident(g12,g13)
    c: Coincident(g13,g14)
    c: Horizontal(g11)
    c: Horizontal(g13)
    c: Vertical(g12)
    c: Vertical(g14)
    c: DistanceY(g2,g11) = 27
    c: DistanceX(g11,g2) = 19
    c: Coincident(g14,g11)
    c: DistanceY(g14,g14) = 80
    c: DistanceX(g13,g13) = 114.6
    c: DistanceY(g2,g10) = 0.4
    c: Coincident(g10,g15)
    c: Horizontal(g15)
    c: Coincident(g15,g16)
    c: Vertical(g16)
    c: Coincident(g16,g17)
    c: Horizontal(g17)
    c: PointOnObject(g9,g2)
    c: DistanceX(g16,g11) = 0
    c: DistanceY(g16,g11) = 0.4
    c: DistanceX(g11,g17) = 20
    c: Coincident(g17,g18)
    c: Vertical(g18)
    c: Coincident(g18,g19)
    c: Coincident(g19,g9)
    c: Horizontal(g19)
FEATURE [PartDesign::Pad] Pad
  Direction = (0,0,1)
  Length = 10
  Length2 = 10
  Profile = -> Sketch
  ReferenceAxis = -> Sketch [N_Axis]
  Refine = true
  Suppressed = false
  Type = 0
FEATURE [Sketcher::SketchObject] Sketch001
  ArcFitTolerance = 1e-06
  AttachmentSupport = -> [Pad]
  FullyConstrained = true
  MakeInternals = false
  MapMode = 5
  Placement = pos=(0,0,10) rot=(0,0,1;0rad)
  expr: Constraints[11] = Sketch.Constraints[11]
  expr: Constraints[12] = Sketch.Constraints[12]
  expr: Constraints[13] = Sketch.Constraints[13]
  expr: Constraints[15] = Sketch.Constraints[15]
  expr: Constraints[16] = Sketch.Constraints[16]
  expr: Constraints[17] = Sketch.Constraints[17]
  expr: Constraints[18] = Sketch.Constraints[18]
  expr: Constraints[19] = Sketch.Constraints[19]
  expr: Constraints[20] = Sketch.Constraints[20]
  expr: Constraints[22] = Sketch.Constraints[22]
  expr: Constraints[31] = Sketch.Constraints[28]
  expr: Constraints[34] = Sketch.Constraints[30]
  expr: Constraints[8] = Sketch.Constraints[8]
  expr: Constraints[9] = Sketch.Constraints[9]
  sketch-geometry (14):
    g0: LineSegment [constr] StartX=0 StartY=0 StartZ=0 EndX=178 EndY=0 EndZ=0
    g1: LineSegment [constr] StartX=178 StartY=0 StartZ=0 EndX=178 EndY=70 EndZ=0
    g2: LineSegment [constr] StartX=178 StartY=70 StartZ=0 EndX=0 EndY=70 EndZ=0
    g3: LineSegment [constr] StartX=0 StartY=70 StartZ=0 EndX=0 EndY=0 EndZ=0
    g4: Circle [constr] CenterX=15 CenterY=60 CenterZ=0 NormalX=0 NormalY=0 NormalZ=1 AngleXU=0 Radius=4.3
    g5: Circle [constr] CenterX=15 CenterY=10 CenterZ=0 NormalX=0 NormalY=0 NormalZ=1 AngleXU=0 Radius=4.3
    g6: Circle [constr] CenterX=170 CenterY=47 CenterZ=0 NormalX=0 NormalY=0 NormalZ=1 AngleXU=0 Radius=2.8
    g7: Circle [constr] CenterX=170 CenterY=23 CenterZ=0 NormalX=0 NormalY=0 NormalZ=1 AngleXU=0 Radius=2.8
    g8: LineSegment [constr] StartX=0.4 StartY=0 StartZ=0 EndX=177.6 EndY=0 EndZ=0
    g9: LineSegment [constr] StartX=177.6 StartY=0 StartZ=0 EndX=177.6 EndY=70 EndZ=0
    g10: LineSegment [constr] StartX=177.6 StartY=70 StartZ=0 EndX=0.4 EndY=70 EndZ=0
    g11: LineSegment [constr] StartX=0.4 StartY=70 StartZ=0 EndX=0.4 EndY=0 EndZ=0
    g12: Circle CenterX=170 CenterY=47 CenterZ=0 NormalX=0 NormalY=0 NormalZ=1 AngleXU=0 Radius=4.5
    g13: Circle CenterX=170 CenterY=23 CenterZ=0 NormalX=0 NormalY=0 NormalZ=1 AngleXU=0 Radius=4.5
  constraints (39):
    c: Coincident(g0,g1)
    c: Coincident(g1,g2)
    c: Coincident(g2,g3)
    c: Coincident(g3,g0)
    c: Horizontal(g0)
    c: Horizontal(g2)
    c: Vertical(g1)
    c: Vertical(g3)
    c: Distance(g1,g3) = 178
    c: Distance(g0,g2) = 70
    c: Coincident(g0,g-1)
    c: DistanceX(g5) = 15
    c: DistanceX(g5,g4) = 0
    c: DistanceY(g5,g4) = 50
    c: Equal(g5,g4)
    c: Diameter(g5) = 8.6
    c: DistanceY(g0,g5) = 10
    c: DistanceX(g7,g0) = 8
    c: DistanceY(g7,g6) = 24
    c: DistanceX(g6,g7) = 0
    c: Diameter(g7) = 5.6
    c: Equal(g7,g6)
    c: DistanceY(g7) = 23
    c: Coincident(g8,g9)
    c: Coincident(g9,g10)
    c: Coincident(g10,g11)
    c: Coincident(g11,g8)
    c: Horizontal(g8)
    c: Horizontal(g10)
    c: Vertical(g9)
    c: Vertical(g11)
    c: DistanceX(g8) = 0.4
    c: PointOnObject(g8,g-1)
    c: PointOnObject(g10,g2)
    c: DistanceX(g8,g0) = 0.4
    c: Coincident(g12,g6)
    c: Coincident(g13,g7)
    c: Diameter(g13) = 9
    c: Equal(g13,g12)
FEATURE [PartDesign::Pocket] Pocket
  BaseFeature = -> Pad
  Direction = (0,0,-1)
  Length = 5
  Length2 = 5
  Profile = -> Sketch001
  ReferenceAxis = -> Sketch001 [N_Axis]
  Refine = true
  Suppressed = false
  Type = 0
FEATURE [PartDesign::Fillet] Fillet
  Base = -> Pocket [Edge30]
  BaseFeature = -> Pocket
  Radius = 4
  Refine = true
  SupportTransform = false
  Suppressed = false
  UseAllEdges = false
FEATURE [Sketcher::SketchObject] Sketch002
  ArcFitTolerance = 1e-06
  AttachmentSupport = -> [Fillet]
  FullyConstrained = true
  MakeInternals = false
  MapMode = 5
  Placement = pos=(0,0,10) rot=(0,0,1;0rad)
  sketch-geometry (20):
    g0: LineSegment [constr] StartX=-19 StartY=96.6 StartZ=0 EndX=95.6 EndY=96.6 EndZ=0
    g1: LineSegment [constr] StartX=95.6 StartY=96.6 StartZ=0 EndX=95.6 EndY=176.6 EndZ=0
    g2: LineSegment [constr] StartX=95.6 StartY=176.6 StartZ=0 EndX=-19 EndY=176.6 EndZ=0
    g3: LineSegment [constr] StartX=-19 StartY=176.6 StartZ=0 EndX=-19 EndY=96.6 EndZ=0
    g4: LineSegment [constr] StartX=-19 StartY=96.6 StartZ=0 EndX=-19 EndY=71.6 EndZ=0
    g5: LineSegment [constr] StartX=-19 StartY=71.6 StartZ=0 EndX=-4 EndY=71.6 EndZ=0
    g6: LineSegment [constr] StartX=-4 StartY=71.6 StartZ=0 EndX=-4 EndY=96.6 EndZ=0
    g7: LineSegment [constr] StartX=11 StartY=96.6 StartZ=0 EndX=11 EndY=71.6 EndZ=0
    g8: LineSegment [constr] StartX=11 StartY=71.6 StartZ=0 EndX=36 EndY=71.6 EndZ=0
    g9: LineSegment [constr] StartX=36 StartY=71.6 StartZ=0 EndX=36 EndY=96.6 EndZ=0
    g10: LineSegment [constr] StartX=95.6 StartY=96.6 StartZ=0 EndX=95.6 EndY=71.6 EndZ=0
    g11: LineSegment [constr] StartX=95.6 StartY=71.6 StartZ=0 EndX=110.6 EndY=71.6 EndZ=0
    g12: LineSegment [constr] StartX=110.6 StartY=71.6 StartZ=0 EndX=110.6 EndY=96.6 EndZ=0
    g13: LineSegment [constr] StartX=110.6 StartY=96.6 StartZ=0 EndX=95.6 EndY=96.6 EndZ=0
    g14: LineSegment [constr] StartX=-19 StartY=96.6 StartZ=0 EndX=-4 EndY=71.6 EndZ=0
    g15: LineSegment [constr] StartX=11 StartY=96.6 StartZ=0 EndX=36 EndY=71.6 EndZ=0
    g16: LineSegment [constr] StartX=95.6 StartY=96.6 StartZ=0 EndX=110.6 EndY=71.6 EndZ=0
    g17: Circle CenterX=-11.5 CenterY=84.1 CenterZ=0 NormalX=0 NormalY=0 NormalZ=1 AngleXU=0 Radius=4.3
    g18: Circle CenterX=23.5 CenterY=84.1 CenterZ=0 NormalX=0 NormalY=0 NormalZ=1 AngleXU=0 Radius=4.3
    g19: Circle CenterX=103.1 CenterY=84.1 CenterZ=0 NormalX=0 NormalY=0 NormalZ=1 AngleXU=0 Radius=4.3
  constraints (54):
    c: Coincident(g0,g1)
    c: Coincident(g1,g2)
    c: Coincident(g2,g3)
    c: Coincident(g3,g0)
    c: Horizontal(g0)
    c: Horizontal(g2)
    c: Vertical(g1)
    c: Vertical(g3)
    c: Distance(g1,g3) = 114.6
    c: Distance(g0,g2) = 80
    c: DistanceY(g0) = 96.6
    c: DistanceX(g0) = -19
    c: Coincident(g0,g4)
    c: Vertical(g4)
    c: Coincident(g4,g5)
    c: Horizontal(g5)
    c: Coincident(g5,g6)
    c: PointOnObject(g6,g0)
    c: Vertical(g6)
    c: PointOnObject(g7,g0)
    c: Vertical(g7)
    c: Coincident(g7,g8)
    c: Horizontal(g8)
    c: Coincident(g8,g9)
    c: PointOnObject(g9,g0)
    c: Vertical(g9)
    c: Coincident(g0,g10)
    c: Vertical(g10)
    c: Coincident(g10,g11)
    c: Horizontal(g11)
    c: Coincident(g11,g12)
    c: Vertical(g12)
    c: Coincident(g12,g13)
    c: Coincident(g13,g10)
    c: Horizontal(g13)
    c: DistanceY(g4,g4) = 25
    c: Equal(g6,g7)
    c: Equal(g7,g10)
    c: DistanceX(g5,g5) = 15
    c: DistanceX(g8,g8) = 25
    c: DistanceX(g0,g7) = 30
    c: DistanceX(g11,g11) = 15
    c: Coincident(g14,g0)
    c: Coincident(g14,g5)
    c: Coincident(g15,g7)
    c: Coincident(g15,g8)
    c: Coincident(g16,g0)
    c: Coincident(g16,g11)
    c: Diameter(g17) = 8.6
    c: Symmetric(g14,g14,g17)
    c: Symmetric(g15,g15,g18)
    c: Symmetric(g16,g16,g19)
    c: Equal(g19,g18)
    c: Equal(g18,g17)
FEATURE [PartDesign::Pocket] Pocket001
  BaseFeature = -> Fillet
  Direction = (0,0,-1)
  Length = 5
  Length2 = 5
  Profile = -> Sketch002
  ReferenceAxis = -> Sketch002 [N_Axis]
  Refine = true
  Suppressed = false
  Type = 1
FEATURE [PartDesign::Body] Body  label="sway_motor_mount_rear_plate"
  AllowCompound = false
  Group = -> [Sketch,Pad,Sketch001,Pocket,Fillet,Sketch002,Pocket001]
  Origin = -> Origin
  Tip = -> Pocket001
COMPONENT P26 — geometry summary ("sway_motor_mount_side"; no construction recipe available for this part):
  bounding box: 130.8 x 81.5 x 80.0 mm
  tessellated surface: 27,392 triangles
  volume: 141936 mm^3 (17% of its bounding box)
COMPONENT P27 — recipe-attached ("sway_motor_mount_top", a linked part whose construction recipe lives in a companion FreeCAD document of the same project; that document's serialized recipe follows).
Construction recipe (the companion document, serialized — sketch geometry with constraints, then the solid features built on it; lengths are millimeters unless a unit is written):

FCSTD DOCUMENT  (FreeCAD 1.0R39109 (Git))
Label: sway_motor_mount_top
License: All rights reserved
LicenseURL: https://en.wikipedia.org/wiki/All_rights_reserved
objects: Sketcher::SketchObject×4, PartDesign::Pocket×3, PartDesign::Fillet×3, PartDesign::Pad×1, PartDesign::Groove×1, PartDesign::Body×1
note: 33 computed .brp shape members not serialized (recipe doc carries the construction recipe); baked Part::Feature solids carry a one-line shape summary decoded from their .brp

FEATURE [Sketcher::SketchObject] Sketch
  ArcFitTolerance = 1e-06
  AttachmentSupport = -> [XZ_Plane]
  FullyConstrained = true
  MakeInternals = false
  MapMode = 5
  Placement = pos=(0,0,0) rot=(1,0,0;1.5708rad)
  sketch-geometry (31):
    g0: LineSegment [constr] StartX=-66.2 StartY=5 StartZ=0 EndX=-66.2 EndY=-5 EndZ=0
    g1: LineSegment [constr] StartX=-66.2 StartY=-5 StartZ=0 EndX=-40 EndY=-5 EndZ=0
    g2: LineSegment [constr] StartX=-40 StartY=-5 StartZ=0 EndX=-40 EndY=5 EndZ=0
    g3: LineSegment [constr] StartX=-40 StartY=5 StartZ=0 EndX=-66.2 EndY=5 EndZ=0
    g4: LineSegment [constr] StartX=40 StartY=5 StartZ=0 EndX=40 EndY=-5 EndZ=0
    g5: LineSegment [constr] StartX=40 StartY=-5 StartZ=0 EndX=66.2 EndY=-5 EndZ=0
    g6: LineSegment [constr] StartX=66.2 StartY=-5 StartZ=0 EndX=66.2 EndY=5 EndZ=0
    g7: LineSegment [constr] StartX=66.2 StartY=5 StartZ=0 EndX=40 EndY=5 EndZ=0
    g8: LineSegment [constr] StartX=-40 StartY=-5 StartZ=0 EndX=0 EndY=0 EndZ=0
    g9: LineSegment [constr] StartX=0 StartY=0 StartZ=0 EndX=40 EndY=-5 EndZ=0
    g10: LineSegment [constr] StartX=-40 StartY=60 StartZ=0 EndX=-40 EndY=-20 EndZ=0
    g11: LineSegment [constr] StartX=-40 StartY=-20 StartZ=0 EndX=40 EndY=-20 EndZ=0
    g12: LineSegment [constr] StartX=40 StartY=-20 StartZ=0 EndX=40 EndY=60 EndZ=0
    g13: LineSegment [constr] StartX=40 StartY=60 StartZ=0 EndX=-40 EndY=60 EndZ=0
    g14: ArcOfCircle [constr] CenterX=-40 CenterY=-20 CenterZ=0 NormalX=0 NormalY=0 NormalZ=1 AngleXU=0 Radius=14 StartAngle=0 EndAngle=1.5708
    g15: ArcOfCircle [constr] CenterX=-40 CenterY=60 CenterZ=0 NormalX=0 NormalY=0 NormalZ=1 AngleXU=0 Radius=14 StartAngle=4.71239 EndAngle=6.28319
    g16: ArcOfCircle [constr] CenterX=40 CenterY=-20 CenterZ=0 NormalX=0 NormalY=0 NormalZ=1 AngleXU=0 Radius=14 StartAngle=1.5708 EndAngle=3.14159
    g17: ArcOfCircle [constr] CenterX=40 CenterY=60 CenterZ=0 NormalX=0 NormalY=0 NormalZ=1 AngleXU=0 Radius=14 StartAngle=3.14159 EndAngle=4.71239
    g18: ArcOfCircle CenterX=-40.4 CenterY=60.4 CenterZ=0 NormalX=0 NormalY=0 NormalZ=1 AngleXU=0 Radius=14 StartAngle=4.71239 EndAngle=6.28319
    g19: ArcOfCircle CenterX=40.4 CenterY=60.4 CenterZ=0 NormalX=0 NormalY=0 NormalZ=1 AngleXU=0 Radius=14 StartAngle=3.14159 EndAngle=4.71239
    g20: LineSegment StartX=-40.4 StartY=5.4 StartZ=0 EndX=-65.4 EndY=5.4 EndZ=0
    g21: LineSegment StartX=-65.4 StartY=5.4 StartZ=0 EndX=-65.4 EndY=15.4 EndZ=0
    g22: LineSegment StartX=-65.4 StartY=15.4 StartZ=0 EndX=-34.5532 EndY=65.4 EndZ=0
    g23: LineSegment StartX=-34.5532 StartY=65.4 StartZ=0 EndX=34.5532 EndY=65.4 EndZ=0
    g24: LineSegment StartX=34.5532 StartY=65.4 StartZ=0 EndX=65.4 EndY=15.4 EndZ=0
    g25: LineSegment StartX=65.4 StartY=15.4 StartZ=0 EndX=65.4 EndY=5.4 EndZ=0
    g26: LineSegment StartX=65.4 StartY=5.4 StartZ=0 EndX=40.4 EndY=5.4 EndZ=0
    g27: LineSegment StartX=40.4 StartY=5.4 StartZ=0 EndX=40.4 EndY=46.4 EndZ=0
    g28: LineSegment StartX=-26.4 StartY=60.4 StartZ=0 EndX=26.4 EndY=60.4 EndZ=0
    g29: LineSegment StartX=-40.4 StartY=46.4 StartZ=0 EndX=-40.4 EndY=5.4 EndZ=0
    g30: LineSegment [constr] StartX=-44.6553 StartY=49.0253 StartZ=0 EndX=-40.4 EndY=46.4 EndZ=0
  constraints (97):
    c: Coincident(g0,g1)
    c: Coincident(g1,g2)
    c: Coincident(g2,g3)
    c: Coincident(g3,g0)
    c: Vertical(g0)
    c: Vertical(g2)
    c: Horizontal(g1)
    c: Horizontal(g3)
    c: Coincident(g4,g5)
    c: Coincident(g5,g6)
    c: Coincident(g6,g7)
    c: Coincident(g7,g4)
    c: Vertical(g4)
    c: Vertical(g6)
    c: Horizontal(g5)
    c: Horizontal(g7)
    c: Equal(g2,g4)
    c: DistanceY(g0,g0) = 10
    c: DistanceX(g2,g4) = 80
    c: DistanceY(g2,g4) = 0
    c: Coincident(g8,g1)
    c: Coincident(g8,g-1)
    c: Coincident(g9,g8)
    c: Coincident(g9,g4)
    c: Equal(g9,g8)
    c: Coincident(g10,g11)
    c: Coincident(g11,g12)
    c: Coincident(g12,g13)
    c: Coincident(g13,g10)
    c: Vertical(g10)
    c: Vertical(g12)
    c: Horizontal(g11)
    c: Horizontal(g13)
    c: PointOnObject(g2,g10)
    c: PointOnObject(g4,g12)
    c: Equal(g13,g10)
    c: DistanceY(g2,g10) = 55
    c: DistanceY(g2) = 5
    c: Coincident(g14,g10)
    c: PointOnObject(g14,g10)
    c: PointOnObject(g14,g11)
    c: Diameter(g14) = 28
    c: Coincident(g15,g10)
    c: PointOnObject(g15,g13)
    c: PointOnObject(g15,g10)
    c: Coincident(g16,g11)
    c: PointOnObject(g16,g11)
    c: PointOnObject(g16,g12)
    c: Coincident(g17,g12)
    c: PointOnObject(g17,g13)
    c: PointOnObject(g17,g12)
    c: Equal(g14,g16)
    c: Equal(g16,g17)
    c: Equal(g17,g15)
    c: Horizontal(g20)
    c: Coincident(g20,g21)
    c: Vertical(g21)
    c: Coincident(g21,g22)
    c: Coincident(g22,g23)
    c: Horizontal(g23)
    c: Coincident(g23,g24)
    c: Coincident(g24,g25)
    c: Vertical(g25)
    c: Coincident(g25,g26)
    c: Horizontal(g26)
    c: Coincident(g26,g27)
    c: Coincident(g27,g19)
    c: Vertical(g27)
    c: Coincident(g28,g18)
    c: Coincident(g28,g19)
    c: Horizontal(g28)
    c: Coincident(g29,g18)
    c: Coincident(g29,g20)
    c: Vertical(g29)
    c: DistanceY(g0,g20) = 0.4
    c: DistanceX(g20,g2) = 0.4
    c: Perpendicular(g18,g29)
    c: DistanceY(g15,g18) = 0.4
    c: Perpendicular(g18,g28)
    c: DistanceY(g18,g22) = 5
    c: DistanceY(g20,g21) = 10
    c: Equal(g21,g25)
    c: Equal(g22,g24)
    c: DistanceX(g4,g26) = 0.4
    c: DistanceY(g4,g26) = 0.4
    c: Equal(g27,g29)
    c: Perpendicular(g19,g27)
    c: Perpendicular(g19,g28)
    c: DistanceY(g15,g18) = 0.4
    c: Equal(g3,g7)
    c: DistanceX(g1,g1) = 26.2
    c: DistanceX(g20,g20) = 25
    c: Equal(g26,g20)
    c: PointOnObject(g30,g22)
    c: Coincident(g30,g18)
    c: Perpendicular(g22,g30)
    c: Distance(g30) = 5
FEATURE [PartDesign::Pad] Pad
  Direction = (0,-1,2e-16)
  Length = 15
  Length2 = 10
  Placement = pos=(0,0,0) rot=(1,0,0;1.5708rad)
  Profile = -> Sketch
  ReferenceAxis = -> Sketch [N_Axis]
  Refine = true
  Suppressed = false
  Type = 0
FEATURE [Sketcher::SketchObject] Sketch001
  ArcFitTolerance = 1e-06
  AttachmentSupport = -> [Pad]
  FullyConstrained = true
  MakeInternals = false
  MapMode = 5
  Placement = pos=(0,2.4e-15,5.4) rot=(1,0,0;3.14159rad)
  sketch-geometry (14):
    g0: LineSegment [constr] StartX=-65.4 StartY=1.8e-15 StartZ=0 EndX=-40.4 EndY=1.8e-15 EndZ=0
    g1: LineSegment [constr] StartX=-40.4 StartY=1.8e-15 StartZ=0 EndX=-40.4 EndY=15 EndZ=0
    g2: LineSegment [constr] StartX=-40.4 StartY=15 StartZ=0 EndX=-65.4 EndY=15 EndZ=0
    g3: LineSegment [constr] StartX=-65.4 StartY=15 StartZ=0 EndX=-65.4 EndY=1.8e-15 EndZ=0
    g4: LineSegment [constr] StartX=65.4 StartY=0 StartZ=0 EndX=65.4 EndY=15 EndZ=0
    g5: LineSegment [constr] StartX=65.4 StartY=15 StartZ=0 EndX=40.4 EndY=15 EndZ=0
    g6: LineSegment [constr] StartX=40.4 StartY=15 StartZ=0 EndX=40.4 EndY=0 EndZ=0
    g7: LineSegment [constr] StartX=40.4 StartY=0 StartZ=0 EndX=65.4 EndY=0 EndZ=0
    g8: LineSegment [constr] StartX=-65.4 StartY=15 StartZ=0 EndX=-40.4 EndY=3.6e-15 EndZ=0
    g9: LineSegment [constr] StartX=-65.4 StartY=1.8e-15 StartZ=0 EndX=-40.4 EndY=15 EndZ=0
    g10: LineSegment [constr] StartX=40.4 StartY=15 StartZ=0 EndX=65.4 EndY=3.6e-15 EndZ=0
    g11: LineSegment [constr] StartX=40.4 StartY=0 StartZ=0 EndX=65.4 EndY=15 EndZ=0
    g12: Circle CenterX=-52.9 CenterY=7.5 CenterZ=0 NormalX=0 NormalY=0 NormalZ=1 AngleXU=0 Radius=4.3
    g13: Circle CenterX=52.9 CenterY=7.5 CenterZ=0 NormalX=0 NormalY=0 NormalZ=1 AngleXU=0 Radius=4.3
  constraints (36):
    c: Coincident(g0,g1)
    c: Coincident(g1,g2)
    c: Coincident(g2,g3)
    c: Coincident(g3,g0)
    c: Horizontal(g0)
    c: Horizontal(g2)
    c: Vertical(g1)
    c: Vertical(g3)
    c: Distance(g1,g3) = 25
    c: Distance(g0,g2) = 15
    c: PointOnObject(g0,g-1)
    c: DistanceX(g0) = -40.4
    c: Coincident(g4,g5)
    c: Coincident(g5,g6)
    c: Coincident(g6,g7)
    c: Coincident(g7,g4)
    c: Vertical(g4)
    c: Vertical(g6)
    c: Horizontal(g5)
    c: Horizontal(g7)
    c: PointOnObject(g4,g-1)
    c: DistanceX(g6) = 40.4
    c: Coincident(g8,g2)
    c: Coincident(g8,g0)
    c: Coincident(g9,g0)
    c: Coincident(g9,g1)
    c: Coincident(g10,g5)
    c: Coincident(g10,g4)
    c: Coincident(g11,g6)
    c: Coincident(g11,g4)
    c: Diameter(g12) = 8.6
    c: Symmetric(g8,g8,g12)
    c: Symmetric(g11,g11,g13)
    c: Equal(g2,g5)
    c: Equal(g3,g4)
    c: Equal(g12,g13)
FEATURE [PartDesign::Pocket] Pocket
  BaseFeature = -> Pad
  Direction = (0,0,1)
  Length = 5
  Length2 = 5
  Placement = pos=(0,0,0) rot=(1,0,0;1.5708rad)
  Profile = -> Sketch001
  ReferenceAxis = -> Sketch001 [N_Axis]
  Refine = true
  Suppressed = false
  Type = 1
FEATURE [Sketcher::SketchObject] Sketch002
  ArcFitTolerance = 1e-06
  AttachmentOffset = pos=(0,0,-5) rot=(0,0,1;0rad)
  AttachmentSupport = -> [Pocket]
  FullyConstrained = true
  MakeInternals = false
  MapMode = 5
  Placement = pos=(0,2.4e-15,10.4) rot=(1,0,0;3.14159rad)
  expr: Constraints[11] = Sketch001.Constraints[11]
  expr: Constraints[21] = Sketch001.Constraints[21]
  expr: Constraints[30] = Sketch001.Constraints[30]
  expr: Constraints[8] = Sketch001.Constraints[8]
  expr: Constraints[9] = Sketch001.Constraints[9]
  sketch-geometry (16):
    g0: LineSegment [constr] StartX=-65.4 StartY=0 StartZ=0 EndX=-40.4 EndY=0 EndZ=0
    g1: LineSegment [constr] StartX=-40.4 StartY=0 StartZ=0 EndX=-40.4 EndY=15 EndZ=0
    g2: LineSegment [constr] StartX=-40.4 StartY=15 StartZ=0 EndX=-65.4 EndY=15 EndZ=0
    g3: LineSegment [constr] StartX=-65.4 StartY=15 StartZ=0 EndX=-65.4 EndY=0 EndZ=0
    g4: LineSegment [constr] StartX=65.4 StartY=0 StartZ=0 EndX=65.4 EndY=15 EndZ=0
    g5: LineSegment [constr] StartX=65.4 StartY=15 StartZ=0 EndX=40.4 EndY=15 EndZ=0
    g6: LineSegment [constr] StartX=40.4 StartY=15 StartZ=0 EndX=40.4 EndY=0 EndZ=0
    g7: LineSegment [constr] StartX=40.4 StartY=0 StartZ=0 EndX=65.4 EndY=0 EndZ=0
    g8: LineSegment [constr] StartX=-65.4 StartY=15 StartZ=0 EndX=-40.4 EndY=3.6e-15 EndZ=0
    g9: LineSegment [constr] StartX=-65.4 StartY=0 StartZ=0 EndX=-40.4 EndY=15 EndZ=0
    g10: LineSegment [constr] StartX=40.4 StartY=15 StartZ=0 EndX=65.4 EndY=3.6e-15 EndZ=0
    g11: LineSegment [constr] StartX=40.4 StartY=0 StartZ=0 EndX=65.4 EndY=15 EndZ=0
    g12: Circle [constr] CenterX=-52.9 CenterY=7.5 CenterZ=0 NormalX=0 NormalY=0 NormalZ=1 AngleXU=0 Radius=4.3
    g13: Circle [constr] CenterX=52.9 CenterY=7.5 CenterZ=0 NormalX=0 NormalY=0 NormalZ=1 AngleXU=0 Radius=4.3
    g14: Circle CenterX=-52.9 CenterY=7.5 CenterZ=0 NormalX=0 NormalY=0 NormalZ=1 AngleXU=0 Radius=6.75
    g15: Circle CenterX=52.9 CenterY=7.5 CenterZ=0 NormalX=0 NormalY=0 NormalZ=1 AngleXU=0 Radius=6.75
  constraints (40):
    c: Coincident(g0,g1)
    c: Coincident(g1,g2)
    c: Coincident(g2,g3)
    c: Coincident(g3,g0)
    c: Horizontal(g0)
    c: Horizontal(g2)
    c: Vertical(g1)
    c: Vertical(g3)
    c: Distance(g1,g3) = 25
    c: Distance(g0,g2) = 15
    c: PointOnObject(g0,g-1)
    c: DistanceX(g0) = -40.4
    c: Coincident(g4,g5)
    c: Coincident(g5,g6)
    c: Coincident(g6,g7)
    c: Coincident(g7,g4)
    c: Vertical(g4)
    c: Vertical(g6)
    c: Horizontal(g5)
    c: Horizontal(g7)
    c: PointOnObject(g4,g-1)
    c: DistanceX(g6) = 40.4
    c: Coincident(g8,g2)
    c: Coincident(g8,g0)
    c: Coincident(g9,g0)
    c: Coincident(g9,g1)
    c: Coincident(g10,g5)
    c: Coincident(g10,g4)
    c: Coincident(g11,g6)
    c: Coincident(g11,g4)
    c: Diameter(g12) = 8.6
    c: Symmetric(g8,g8,g12)
    c: Symmetric(g11,g11,g13)
    c: Equal(g13,g12)
    c: Coincident(g14,g12)
    c: Coincident(g15,g13)
    c: Equal(g14,g15)
    c: Diameter(g14) = 13.5
    c: Equal(g4,g3)
    c: Equal(g5,g2)
FEATURE [PartDesign::Pocket] Pocket001
  BaseFeature = -> Pocket
  Direction = (0,0,1)
  Length = 5
  Length2 = 5
  Placement = pos=(0,0,0) rot=(1,0,0;1.5708rad)
  Profile = -> Sketch002
  ReferenceAxis = -> Sketch002 [N_Axis]
  Refine = true
  Suppressed = false
  Type = 1
FEATURE [PartDesign::Fillet] Fillet
  Base = -> Pocket001 [Edge27,Edge18,Edge23,Edge14]
  BaseFeature = -> Pocket001
  Placement = pos=(0,0,0) rot=(1,0,0;1.5708rad)
  Radius = 4
  Refine = true
  SupportTransform = false
  Suppressed = false
  UseAllEdges = false
FEATURE [PartDesign::Fillet] Fillet001
  Base = -> Fillet [Edge30,Edge23]
  BaseFeature = -> Fillet
  Placement = pos=(0,0,0) rot=(1,0,0;1.5708rad)
  Radius = 18
  Refine = true
  SupportTransform = false
  Suppressed = false
  UseAllEdges = false
FEATURE [Sketcher::SketchObject] Sketch003
  ArcFitTolerance = 1e-06
  AttachmentSupport = -> [Fillet001]
  FullyConstrained = true
  MakeInternals = false
  MapMode = 5
  Placement = pos=(0,-15,0) rot=(1,0,0;1.5708rad)
  sketch-geometry (4):
    g0: ArcOfCircle CenterX=-7 CenterY=65.4 CenterZ=0 NormalX=0 NormalY=0 NormalZ=1 AngleXU=0 Radius=3 StartAngle=3.14159 EndAngle=4.71239
    g1: ArcOfCircle CenterX=7 CenterY=65.4 CenterZ=0 NormalX=0 NormalY=0 NormalZ=1 AngleXU=0 Radius=3 StartAngle=4.71239 EndAngle=6.28319
    g2: LineSegment StartX=-7 StartY=62.4 StartZ=0 EndX=7 EndY=62.4 EndZ=0
    g3: LineSegment StartX=-10 StartY=65.4 StartZ=0 EndX=10 EndY=65.4 EndZ=0
  constraints (12):
    c: Coincident(g3,g0)
    c: Coincident(g3,g1)
    c: Horizontal(g3)
    c: Horizontal(g2)
    c: PointOnObject(g1,g3)
    c: PointOnObject(g0,g3)
    c: Tangent(g2,g1) = -1.5708
    c: Tangent(g2,g0) = -1.5708
    c: DistanceX(g3,g3) = 20
    c: DistanceX(g0) = -10
    c: DistanceY(g0) = 65.4
    c: DistanceY(g0,g0) = 3
FEATURE [PartDesign::Pocket] Pocket002
  BaseFeature = -> Fillet001
  Direction = (0,1,-2e-16)
  Length = 3
  Length2 = 5
  Placement = pos=(0,0,0) rot=(1,0,0;1.5708rad)
  Profile = -> Sketch003
  ReferenceAxis = -> Sketch003 [N_Axis]
  Refine = true
  Suppressed = false
  Type = 0
FEATURE [PartDesign::Groove] Groove
  Angle = 90
  Angle2 = 60
  Axis = (1,0,0)
  Base = (-10,-12,65.4)
  BaseFeature = -> Pocket002
  Placement = pos=(0,0,0) rot=(1,0,0;1.5708rad)
  Profile = -> Pocket002 [Face21]
  ReferenceAxis = -> Pocket002 [Edge27]
  Refine = true
  Suppressed = false
  Type = 0
FEATURE [PartDesign::Fillet] Fillet002
  Base = -> Groove [Edge28]
  BaseFeature = -> Groove
  Placement = pos=(0,0,0) rot=(1,0,0;1.5708rad)
  Radius = 3
  Refine = true
  SupportTransform = false
  Suppressed = false
  UseAllEdges = false
FEATURE [PartDesign::Body] Body  label="sway_motor_mount_top"
  AllowCompound = false
  Group = -> [Sketch,Pad,Sketch001,Pocket,Sketch002,Pocket001,Fillet,Fillet001,Sketch003,Pocket002,Groove,Fillet002]
  Origin = -> Origin
  Tip = -> Fillet002
PROVENANCE & LICENSES
A FreeCAD (.FCStd) document from a public repository crawl; recipes are the document's own serialized feature recipes (and, for linked parts, companion documents' recipes).
License: as declared in the source repository (recorded in the dataset sidecar).
